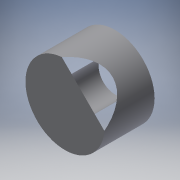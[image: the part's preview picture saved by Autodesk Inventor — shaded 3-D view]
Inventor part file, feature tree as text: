
AUTODESK INVENTOR PART (.ipt)
format: ipt  version: 2016 (Build 200138000, 138)  size: 98,304 bytes
history: native  units: in
note: dims shown in document units (in); Inventor stores cm internally (conversion verified against a paired STEP export)
features: extrude x2, sketch x2, reference x1
ambient origin geometry x8: Origin, YZ Plane, XZ Plane, XY Plane, X Axis, Y Axis, Z Axis, Center Point
bodies: Solid1 (feature_tree)
feature tree (5):
  extrude  "Extrusion1"  Depth=0.3937in
  extrude  "Extrusion2"  [1 undecoded]
  sketch  "Sketch1"  dims[d0=0.601in d1=0.0in d2=0.3937in]
  reference  "Reference1"
  sketch  "Sketch2"  dims[d3=0.3937in d4=0.0in]
note: 1 required parameter value undecoded (feature->parameter linkage not recoverable at this tier; creation-order binding heuristic only, values carry confidence <= 0.55)
